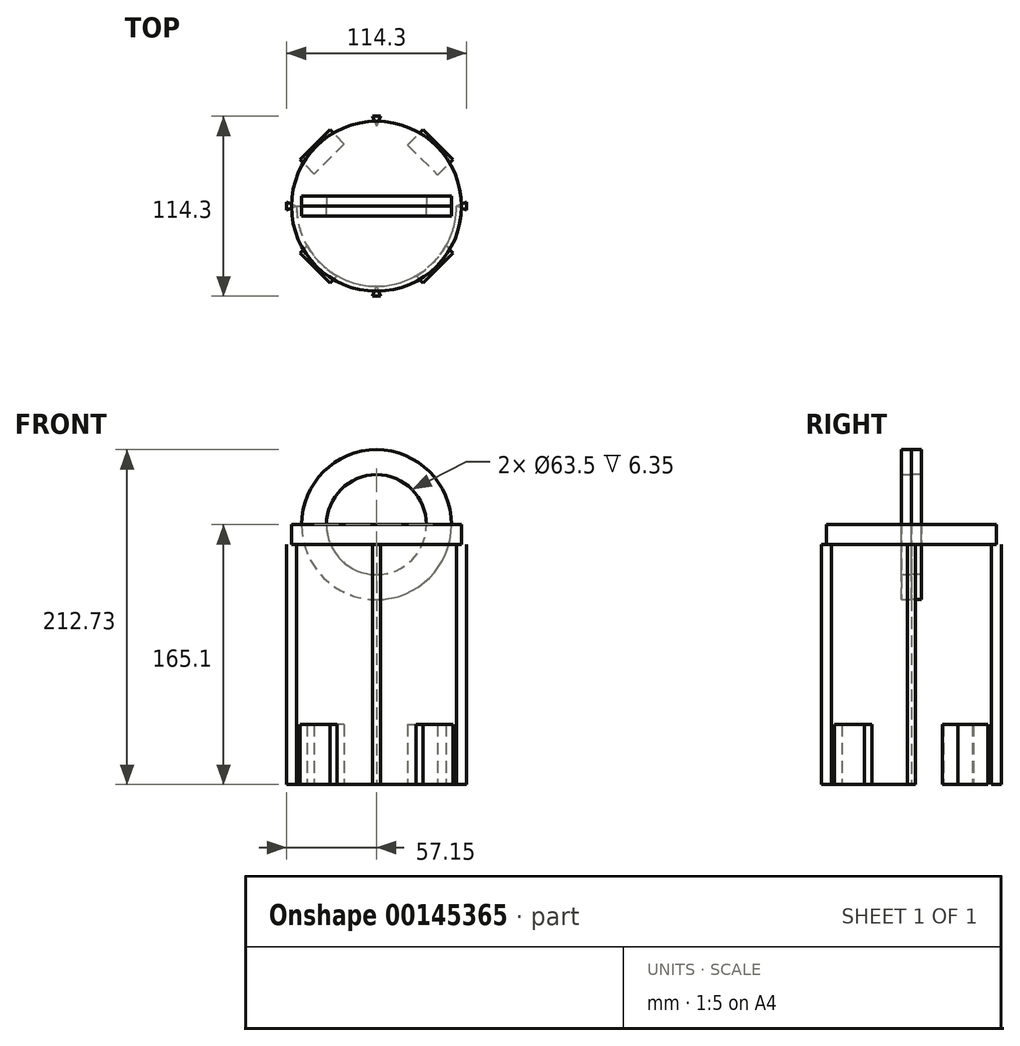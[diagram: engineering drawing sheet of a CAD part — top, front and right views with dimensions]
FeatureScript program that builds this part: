
annotation { "Feature Type Name" : "Feature", "Feature Type Description" : "" }
export const myFeature = defineFeature(function(context is Context, id is Id, definition is map)
    precondition{}
    {
        {
            var Q0;
            Q0=qCreatedBy(makeId("Top.planeOp"),FACE);
            var sketch = newSketch(context, id + "F0", { "sketchPlane" : qUnion([Q0])});
            skCircle(sketch, "E0", {"center": v(0, 0) * mm, "radius": 50.8 * mm});
            skLineSegment(sketch, "E1", {"start": v(0, 0) * mm, "end": v(0, 50.8) * mm});
            skLineSegment(sketch, "E2", {"start": v(0, 50.8) * mm, "end": v(0, 0) * mm});
            skLineSegment(sketch, "E3", {"start": v(50.8, 0) * mm, "end": v(0, 0) * mm});
            skLineSegment(sketch, "E4", {"start": v(0, -50.8) * mm, "end": v(0, 0) * mm});
            skLineSegment(sketch, "E5", {"start": v(-50.8, 0) * mm, "end": v(0, 0) * mm});
            skSolve(sketch);
        }
        {
            var Q0;
            {var subQ0=sQuery(id+"F0.wireOp",EDGE,"E2");Q0=makeQuery(id+"F0.imprint","IMPRINT",FACE,{"disambiguationData":[TD([[makeQuery(id+"F0.imprint","IMPRINT",EDGE,{"derivedFrom":subQ0}),1.0]])]});}
            var Q1;
            {var subQ0=sQuery(id+"F0.wireOp",EDGE,"E4");Q1=makeQuery(id+"F0.imprint","IMPRINT",FACE,{"disambiguationData":[TD([[makeQuery(id+"F0.imprint","IMPRINT",EDGE,{"derivedFrom":subQ0}),1.0]])]});}
            var Q2;
            {var subQ0=sQuery(id+"F0.wireOp",EDGE,"E3");Q2=makeQuery(id+"F0.imprint","IMPRINT",FACE,{"disambiguationData":[TD([[makeQuery(id+"F0.imprint","IMPRINT",EDGE,{"derivedFrom":subQ0}),1.0]])]});}
            var Q3;
            {var subQ0=sQuery(id+"F0.wireOp",EDGE,"E2");Q3=makeQuery(id+"F0.imprint","IMPRINT",FACE,{"disambiguationData":[TD([[makeQuery(id+"F0.imprint","IMPRINT",EDGE,{"derivedFrom":subQ0}),-1.0]])]});}
            extrude(context, id + "F1", {"entities" : qUnion([Q0, Q1, Q2, Q3]), "depth" : 152.4 * mm});
        }
        {
            var Q0;
            Q0=makeQuery(id+"F1.opExtrude","CAP_FACE",FACE,{"disambiguationData":[OSD([sQuery(id+"F0.wireOp",EDGE,"E0")])],"isStart":false});
            var sketch = newSketch(context, id + "F2", { "sketchPlane" : qUnion([Q0])});
            skCircle(sketch, "E6", {"center": v(0, 0) * mm, "radius": 53.97 * mm});
            skSolve(sketch);
        }
        {
            var Q0;
            Q0=qCreatedBy(makeId("Top.planeOp"),FACE);
            var sketch = newSketch(context, id + "F3", { "sketchPlane" : qUnion([Q0])});
            skLineSegment(sketch, "E7", {"start": v(0, 0) * mm, "end": v(0, -19.05) * mm});
            skLineSegment(sketch, "E8", {"start": v(0, 0) * mm, "end": v(0, 19.05) * mm});
            skLineSegment(sketch, "E9", {"start": v(0, 0) * mm, "end": v(-19.05, 0) * mm});
            skLineSegment(sketch, "E10", {"start": v(0, 0) * mm, "end": v(19.05, 0) * mm});
            skLineSegment(sketch, "E11", {"start": v(-19.05, 0) * mm, "end": v(0, 19.05) * mm});
            skLineSegment(sketch, "E12", {"start": v(0, 19.05) * mm, "end": v(19.05, 0) * mm});
            skLineSegment(sketch, "E13", {"start": v(0, -19.05) * mm, "end": v(19.05, 0) * mm});
            skLineSegment(sketch, "E14", {"start": v(-19.05, 0) * mm, "end": v(0, -19.05) * mm});
            skLineSegment(sketch, "E15", {"start": v(0, -19.05) * mm, "end": v(-29.63, -48.68) * mm});
            skLineSegment(sketch, "E16", {"start": v(-19.05, 0) * mm, "end": v(-48.68, -29.63) * mm});
            skLineSegment(sketch, "E17", {"start": v(-48.68, -29.63) * mm, "end": v(-19.05, 0) * mm});
            skLineSegment(sketch, "E18", {"start": v(-19.05, 0) * mm, "end": v(-48.68, 29.63) * mm});
            skLineSegment(sketch, "E19", {"start": v(-48.68, 29.63) * mm, "end": v(-19.05, 0) * mm});
            skLineSegment(sketch, "E20", {"start": v(0, 19.05) * mm, "end": v(-29.63, 48.68) * mm});
            skLineSegment(sketch, "E21", {"start": v(-29.63, 48.68) * mm, "end": v(0, 19.05) * mm});
            skLineSegment(sketch, "E22", {"start": v(0, 19.05) * mm, "end": v(29.63, 48.68) * mm});
            skLineSegment(sketch, "E23", {"start": v(29.63, 48.68) * mm, "end": v(0, 19.05) * mm});
            skLineSegment(sketch, "E24", {"start": v(19.05, 0) * mm, "end": v(48.68, 29.63) * mm});
            skLineSegment(sketch, "E25", {"start": v(48.68, 29.63) * mm, "end": v(19.05, 0) * mm});
            skLineSegment(sketch, "E26", {"start": v(19.05, 0) * mm, "end": v(48.68, -29.63) * mm});
            skLineSegment(sketch, "E27", {"start": v(48.68, -29.63) * mm, "end": v(19.05, 0) * mm});
            skLineSegment(sketch, "E28", {"start": v(0, -19.05) * mm, "end": v(29.63, -48.68) * mm});
            skLineSegment(sketch, "E29", {"start": v(-48.68, -29.63) * mm, "end": v(-29.63, -48.68) * mm});
            skLineSegment(sketch, "E30", {"start": v(-48.68, 29.63) * mm, "end": v(-29.63, 48.68) * mm});
            skLineSegment(sketch, "E31", {"start": v(48.68, 29.63) * mm, "end": v(29.63, 48.68) * mm});
            skLineSegment(sketch, "E32", {"start": v(48.68, -29.63) * mm, "end": v(29.63, -48.68) * mm});
            skLineSegment(sketch, "E33", {"start": v(-48.68, -29.63) * mm, "end": v(-37.7, -18.64) * mm});
            skLineSegment(sketch, "E34", {"start": v(-37.7, -18.64) * mm, "end": v(-18.64, -37.7) * mm});
            skLineSegment(sketch, "E35", {"start": v(-29.63, 48.68) * mm, "end": v(-20.5, 39.55) * mm});
            skLineSegment(sketch, "E36", {"start": v(-20.5, 39.55) * mm, "end": v(-39.55, 20.5) * mm});
            skLineSegment(sketch, "E37", {"start": v(29.63, 48.68) * mm, "end": v(19.78, 38.83) * mm});
            skLineSegment(sketch, "E38", {"start": v(19.78, 38.83) * mm, "end": v(38.83, 19.78) * mm});
            skLineSegment(sketch, "E39", {"start": v(29.63, -48.68) * mm, "end": v(14.82, -33.87) * mm});
            skLineSegment(sketch, "E40", {"start": v(14.82, -33.87) * mm, "end": v(33.87, -14.82) * mm});
            skSolve(sketch);
        }
        {
            var Q0;
            {var subQ0=sQuery(id+"F3.wireOp",EDGE,"E30");Q0=makeQuery(id+"F3.imprint","IMPRINT",FACE,{"disambiguationData":[TD([[makeQuery(id+"F3.imprint","IMPRINT",EDGE,{"derivedFrom":subQ0}),-1.0]])]});}
            var Q1;
            {var subQ0=sQuery(id+"F3.wireOp",EDGE,"E31");Q1=makeQuery(id+"F3.imprint","IMPRINT",FACE,{"disambiguationData":[TD([[makeQuery(id+"F3.imprint","IMPRINT",EDGE,{"derivedFrom":subQ0}),1.0]])]});}
            var Q2;
            {var subQ0=sQuery(id+"F3.wireOp",EDGE,"E29");Q2=makeQuery(id+"F3.imprint","IMPRINT",FACE,{"disambiguationData":[TD([[makeQuery(id+"F3.imprint","IMPRINT",EDGE,{"derivedFrom":subQ0}),1.0]])]});}
            var Q3;
            {var subQ0=sQuery(id+"F3.wireOp",EDGE,"E32");Q3=makeQuery(id+"F3.imprint","IMPRINT",FACE,{"disambiguationData":[TD([[makeQuery(id+"F3.imprint","IMPRINT",EDGE,{"derivedFrom":subQ0}),-1.0]])]});}
            extrude(context, id + "F4", {"entities" : qUnion([Q0, Q1, Q2, Q3]), "operationType" : NewBodyOperationType.ADD, "depth" : 38.1 * mm});
        }
        {
            var Q0;
            Q0 = qSketchRegion(id + "F2", true);
            extrude(context, id + "F5", {"entities" : qUnion([Q0]), "operationType" : NewBodyOperationType.ADD, "depth" : 12.7 * mm});
        }
        {
            var Q0;
            Q0=qCreatedBy(makeId("Front.planeOp"),FACE);
            var sketch = newSketch(context, id + "F6", { "sketchPlane" : qUnion([Q0])});
            skLineSegment(sketch, "E41", {"start": v(0, 0) * mm, "end": v(0, 165.1) * mm});
            skCircle(sketch, "E42", {"center": v(0, 165.1) * mm, "radius": 47.63 * mm});
            skCircle(sketch, "E43", {"center": v(0, 165.1) * mm, "radius": 31.75 * mm});
            skSolve(sketch);
        }
        {
            var Q0;
            Q0 = qSketchRegion(id + "F6", true);
            extrude(context, id + "F7", {"entities" : qUnion([Q0]), "depth" : 6.35 * mm});
        }
        {
            var Q0;
            Q0=makeQuery(id+"F7.opExtrude","SWEPT_BODY",BODY,{"disambiguationData":[OSD([sQuery(id+"F6.wireOp",EDGE,"E42"),sQuery(id+"F6.wireOp",EDGE,"E43")])]});
            var Q1;
            Q1=qCreatedBy(makeId("Front.planeOp"),FACE);
            mirror(context, id + "F8", {"entities" : qUnion([Q0]), "mirrorPlane" : qUnion([Q1])});
        }
        {
            var Q0;
            Q0=makeQuery(id+"F4.boolean.opBoolean","MERGE",FACE,{"derivedFrom":[makeQuery(id+"F1.opExtrude","CAP_FACE",FACE,{"disambiguationData":[OSD([sQuery(id+"F0.wireOp",EDGE,"E0")])],"isStart":true}),makeQuery(id+"F4.opExtrude","CAP_FACE",FACE,{"disambiguationData":[OSD([sQuery(id+"F3.wireOp",EDGE,"E15"),sQuery(id+"F3.wireOp",EDGE,"E29"),sQuery(id+"F3.wireOp",EDGE,"E33"),sQuery(id+"F3.wireOp",EDGE,"E34")])],"isStart":true}),makeQuery(id+"F4.opExtrude","CAP_FACE",FACE,{"disambiguationData":[OSD([sQuery(id+"F3.wireOp",EDGE,"E19"),sQuery(id+"F3.wireOp",EDGE,"E30"),sQuery(id+"F3.wireOp",EDGE,"E35"),sQuery(id+"F3.wireOp",EDGE,"E36")])],"isStart":true}),makeQuery(id+"F4.opExtrude","CAP_FACE",FACE,{"disambiguationData":[OSD([sQuery(id+"F3.wireOp",EDGE,"E25"),sQuery(id+"F3.wireOp",EDGE,"E31"),sQuery(id+"F3.wireOp",EDGE,"E37"),sQuery(id+"F3.wireOp",EDGE,"E38")])],"isStart":true}),makeQuery(id+"F4.opExtrude","CAP_FACE",FACE,{"disambiguationData":[OSD([sQuery(id+"F3.wireOp",EDGE,"E27"),sQuery(id+"F3.wireOp",EDGE,"E32"),sQuery(id+"F3.wireOp",EDGE,"E39"),sQuery(id+"F3.wireOp",EDGE,"E40")])],"isStart":true})]});
            var sketch = newSketch(context, id + "F9", { "sketchPlane" : qUnion([Q0])});
            skLineSegment(sketch, "E44", {"start": v(0, 0) * mm, "end": v(50.8, 0) * mm});
            skLineSegment(sketch, "E45", {"start": v(50.8, 0) * mm, "end": v(0, 0) * mm});
            skLineSegment(sketch, "E46", {"start": v(0, 50.8) * mm, "end": v(0, 0) * mm});
            skLineSegment(sketch, "E47", {"start": v(0, -50.8) * mm, "end": v(0, 0) * mm});
            skLineSegment(sketch, "E48", {"start": v(0, 0) * mm, "end": v(-50.8, 0) * mm});
            skLineSegment(sketch, "E49", {"start": v(-50.8, 0) * mm, "end": v(-57.15, 0) * mm});
            skLineSegment(sketch, "E50", {"start": v(0, 50.8) * mm, "end": v(0, 57.15) * mm});
            skLineSegment(sketch, "E51", {"start": v(50.8, 0) * mm, "end": v(57.15, 0) * mm});
            skLineSegment(sketch, "E52", {"start": v(0, -50.8) * mm, "end": v(0, -57.15) * mm});
            skLineSegment(sketch, "E53", {"start": v(0, 57.15) * mm, "end": v(2.54, 57.15) * mm});
            skLineSegment(sketch, "E54", {"start": v(0, 57.15) * mm, "end": v(-2.54, 57.15) * mm});
            skLineSegment(sketch, "E55", {"start": v(-57.15, 0) * mm, "end": v(-57.15, 2.54) * mm});
            skLineSegment(sketch, "E56", {"start": v(-57.15, 0) * mm, "end": v(-57.15, -2.54) * mm});
            skLineSegment(sketch, "E57", {"start": v(57.15, 0) * mm, "end": v(57.15, -2.54) * mm});
            skLineSegment(sketch, "E58", {"start": v(57.15, 0) * mm, "end": v(57.15, 2.54) * mm});
            skLineSegment(sketch, "E59", {"start": v(0, -57.15) * mm, "end": v(2.54, -57.15) * mm});
            skLineSegment(sketch, "E60", {"start": v(0, -57.15) * mm, "end": v(-2.54, -57.15) * mm});
            skLineSegment(sketch, "E61", {"start": v(-57.15, 2.54) * mm, "end": v(-50.8, 0) * mm});
            skLineSegment(sketch, "E62", {"start": v(-57.15, -2.54) * mm, "end": v(-50.8, 0) * mm});
            skLineSegment(sketch, "E63", {"start": v(-2.54, 57.15) * mm, "end": v(0, 50.8) * mm});
            skLineSegment(sketch, "E64", {"start": v(57.15, 2.54) * mm, "end": v(50.8, 0) * mm});
            skLineSegment(sketch, "E65", {"start": v(57.15, -2.54) * mm, "end": v(50.8, 0) * mm});
            skLineSegment(sketch, "E66", {"start": v(2.54, -57.15) * mm, "end": v(0, -50.8) * mm});
            skLineSegment(sketch, "E67", {"start": v(-2.54, -57.15) * mm, "end": v(0, -50.8) * mm});
            skLineSegment(sketch, "E68", {"start": v(0, 50.8) * mm, "end": v(2.54, 57.15) * mm});
            skSolve(sketch);
        }
        {
            var Q0;
            Q0=makeQuery(id+"F9.imprint","IMPRINT",FACE,{"disambiguationData":[TD([[makeQuery(id+"F9.imprint","IMPRINT",EDGE,{"derivedFrom":sQuery(id+"F9.wireOp",EDGE,"E52")}),-1.0]])]});
            var Q1;
            Q1=makeQuery(id+"F9.imprint","IMPRINT",FACE,{"disambiguationData":[TD([[makeQuery(id+"F9.imprint","IMPRINT",EDGE,{"derivedFrom":sQuery(id+"F9.wireOp",EDGE,"E52")}),1.0]])]});
            var Q2;
            Q2=makeQuery(id+"F9.imprint","IMPRINT",FACE,{"disambiguationData":[TD([[makeQuery(id+"F9.imprint","IMPRINT",EDGE,{"derivedFrom":sQuery(id+"F9.wireOp",EDGE,"E51")}),-1.0]])]});
            var Q3;
            Q3=makeQuery(id+"F9.imprint","IMPRINT",FACE,{"disambiguationData":[TD([[makeQuery(id+"F9.imprint","IMPRINT",EDGE,{"derivedFrom":sQuery(id+"F9.wireOp",EDGE,"E51")}),1.0]])]});
            var Q4;
            Q4=makeQuery(id+"F9.imprint","IMPRINT",FACE,{"disambiguationData":[TD([[makeQuery(id+"F9.imprint","IMPRINT",EDGE,{"derivedFrom":sQuery(id+"F9.wireOp",EDGE,"E50")}),-1.0]])]});
            var Q5;
            Q5=makeQuery(id+"F9.imprint","IMPRINT",FACE,{"disambiguationData":[TD([[makeQuery(id+"F9.imprint","IMPRINT",EDGE,{"derivedFrom":sQuery(id+"F9.wireOp",EDGE,"E50")}),1.0]])]});
            var Q6;
            Q6=makeQuery(id+"F9.imprint","IMPRINT",FACE,{"disambiguationData":[TD([[makeQuery(id+"F9.imprint","IMPRINT",EDGE,{"derivedFrom":sQuery(id+"F9.wireOp",EDGE,"E49")}),1.0]])]});
            var Q7;
            Q7=makeQuery(id+"F9.imprint","IMPRINT",FACE,{"disambiguationData":[TD([[makeQuery(id+"F9.imprint","IMPRINT",EDGE,{"derivedFrom":sQuery(id+"F9.wireOp",EDGE,"E49")}),-1.0]])]});
            extrude(context, id + "F10", {"entities" : qUnion([Q0, Q1, Q2, Q3, Q4, Q5, Q6, Q7]), "oppositeDirection" : true, "depth" : 152.4 * mm});
        }
    });
